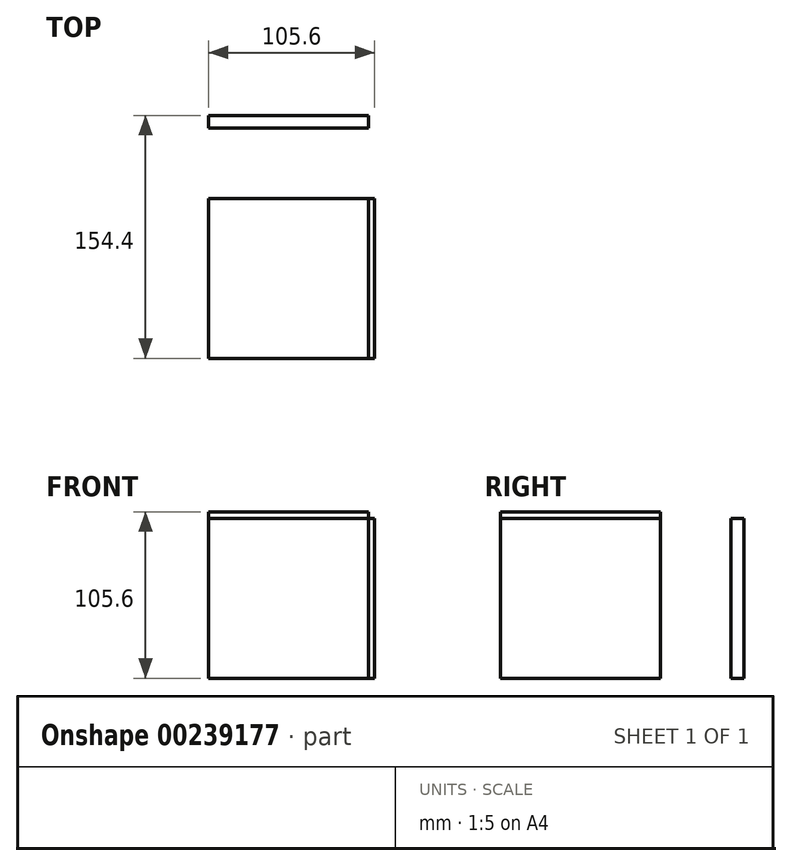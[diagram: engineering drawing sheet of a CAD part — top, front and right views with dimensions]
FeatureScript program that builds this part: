
annotation { "Feature Type Name" : "Feature", "Feature Type Description" : "" }
export const myFeature = defineFeature(function(context is Context, id is Id, definition is map)
    precondition{}
    {
        {
            assignVariable(context, id + "F0", {"name" : "H", "anyValue" : 4});
        }
        {
            var Q0;
            Q0=qCreatedBy(makeId("Front.planeOp"),FACE);
            var sketch = newSketch(context, id + "F1", { "sketchPlane" : qUnion([Q0])});
            skLineSegment(sketch, "E0.bottom", {"start": v(50.8, 50.8) * mm, "end": v(-50.8, 50.8) * mm});
            skLineSegment(sketch, "E0.top", {"start": v(50.8, -50.8) * mm, "end": v(-50.8, -50.8) * mm});
            skLineSegment(sketch, "E0.left", {"start": v(50.8, 50.8) * mm, "end": v(50.8, -50.8) * mm});
            skLineSegment(sketch, "E0.right", {"start": v(-50.8, 50.8) * mm, "end": v(-50.8, -50.8) * mm});
            skPoint(sketch, "E0.middle", {"position": v(0, 0) * mm});
            skSolve(sketch);
        }
        {
            var Q0;
            Q0 = qSketchRegion(id + "F1", true);
            extrude(context, id + "F2", {"entities" : qUnion([Q0]), "endBound" : BoundingType.SYMMETRIC, "depth" : (getVariable(context, 'H')) * mm});
        }
        {
            var Q0;
            Q0=makeQuery(id+"F2.opExtrude","CAP_FACE",FACE,{"disambiguationData":[OSD([sQuery(id+"F1.wireOp",EDGE,"E0.bottom"),sQuery(id+"F1.wireOp",EDGE,"E0.top"),sQuery(id+"F1.wireOp",EDGE,"E0.left"),sQuery(id+"F1.wireOp",EDGE,"E0.right")])],"isStart":false});
            var sketch = newSketch(context, id + "F3", { "sketchPlane" : qUnion([Q0])});
            skLineSegment(sketch, "E1.bottom", {"start": v(-50.8, 50.8) * mm, "end": v(50.8, 50.8) * mm});
            skLineSegment(sketch, "E1.top", {"start": v(-50.8, -50.8) * mm, "end": v(50.8, -50.8) * mm});
            skLineSegment(sketch, "E1.left", {"start": v(-50.8, 50.8) * mm, "end": v(-50.8, -50.8) * mm});
            skLineSegment(sketch, "E1.right", {"start": v(50.8, 50.8) * mm, "end": v(50.8, -50.8) * mm});
            skPoint(sketch, "E1.middle", {"position": v(0, 0) * mm});
            skSolve(sketch);
        }
        {
            var Q0;
            Q0 = qSketchRegion(id + "F3", true);
            extrude(context, id + "F4", {"entities" : qUnion([Q0]), "operationType" : NewBodyOperationType.ADD, "depth" : (getVariable(context, 'H')) * mm});
        }
        {
            var Q0;
            Q0=makeQuery(id+"F4.boolean.opBoolean","MERGE",FACE,{"derivedFrom":[makeQuery(id+"F2.opExtrude","SWEPT_FACE",FACE,{"disambiguationData":[OSD([sQuery(id+"F1.wireOp",EDGE,"E0.left")])]}),makeQuery(id+"F4.opExtrude","SWEPT_FACE",FACE,{"disambiguationData":[OSD([sQuery(id+"F3.wireOp",EDGE,"E1.right")])]})]});
            var sketch = newSketch(context, id + "F5", { "sketchPlane" : qUnion([Q0])});
            skPoint(sketch, "E2.middle", {"position": v(-50.8, 50.8) * mm});
            skLineSegment(sketch, "E3.bottom", {"start": v(-50.8, 50.8) * mm, "end": v(-152.4, 50.8) * mm});
            skLineSegment(sketch, "E3.top", {"start": v(-50.8, -50.8) * mm, "end": v(-152.4, -50.8) * mm});
            skLineSegment(sketch, "E3.left", {"start": v(-50.8, 50.8) * mm, "end": v(-50.8, -50.8) * mm});
            skLineSegment(sketch, "E3.right", {"start": v(-152.4, 50.8) * mm, "end": v(-152.4, -50.8) * mm});
            skSolve(sketch);
        }
        {
            var Q0;
            Q0 = qSketchRegion(id + "F5", true);
            extrude(context, id + "F6", {"entities" : qUnion([Q0]), "operationType" : NewBodyOperationType.ADD, "depth" : (getVariable(context, 'H')) * mm});
        }
        {
            var Q0;
            Q0=makeQuery(id+"F6.boolean.opBoolean","MERGE",FACE,{"derivedFrom":[makeQuery(id+"F4.boolean.opBoolean","MERGE",FACE,{"derivedFrom":[makeQuery(id+"F2.opExtrude","SWEPT_FACE",FACE,{"disambiguationData":[OSD([sQuery(id+"F1.wireOp",EDGE,"E0.bottom")])]}),makeQuery(id+"F4.opExtrude","SWEPT_FACE",FACE,{"disambiguationData":[OSD([sQuery(id+"F3.wireOp",EDGE,"E1.bottom")])]})]}),makeQuery(id+"F6.opExtrude","SWEPT_FACE",FACE,{"disambiguationData":[OSD([sQuery(id+"F5.wireOp",EDGE,"E3.bottom")])]})]});
            var sketch = newSketch(context, id + "F7", { "sketchPlane" : qUnion([Q0])});
            skLineSegment(sketch, "E4.bottom", {"start": v(50.8, -50.8) * mm, "end": v(-50.8, -50.8) * mm});
            skLineSegment(sketch, "E4.top", {"start": v(50.8, -152.4) * mm, "end": v(-50.8, -152.4) * mm});
            skLineSegment(sketch, "E4.left", {"start": v(50.8, -50.8) * mm, "end": v(50.8, -152.4) * mm});
            skLineSegment(sketch, "E4.right", {"start": v(-50.8, -50.8) * mm, "end": v(-50.8, -152.4) * mm});
            skSolve(sketch);
        }
        {
            var Q0;
            Q0=makeQuery(id+"F7.imprint","IMPRINT",FACE,{"disambiguationData":[TD([[makeQuery(id+"F7.imprint","IMPRINT",EDGE,{"derivedFrom":sQuery(id+"F7.wireOp",EDGE,"E4.bottom")}),1.0]])]});
            extrude(context, id + "F8", {"entities" : qUnion([Q0]), "operationType" : NewBodyOperationType.ADD, "depth" : (getVariable(context, 'H')) * mm});
        }
    });
